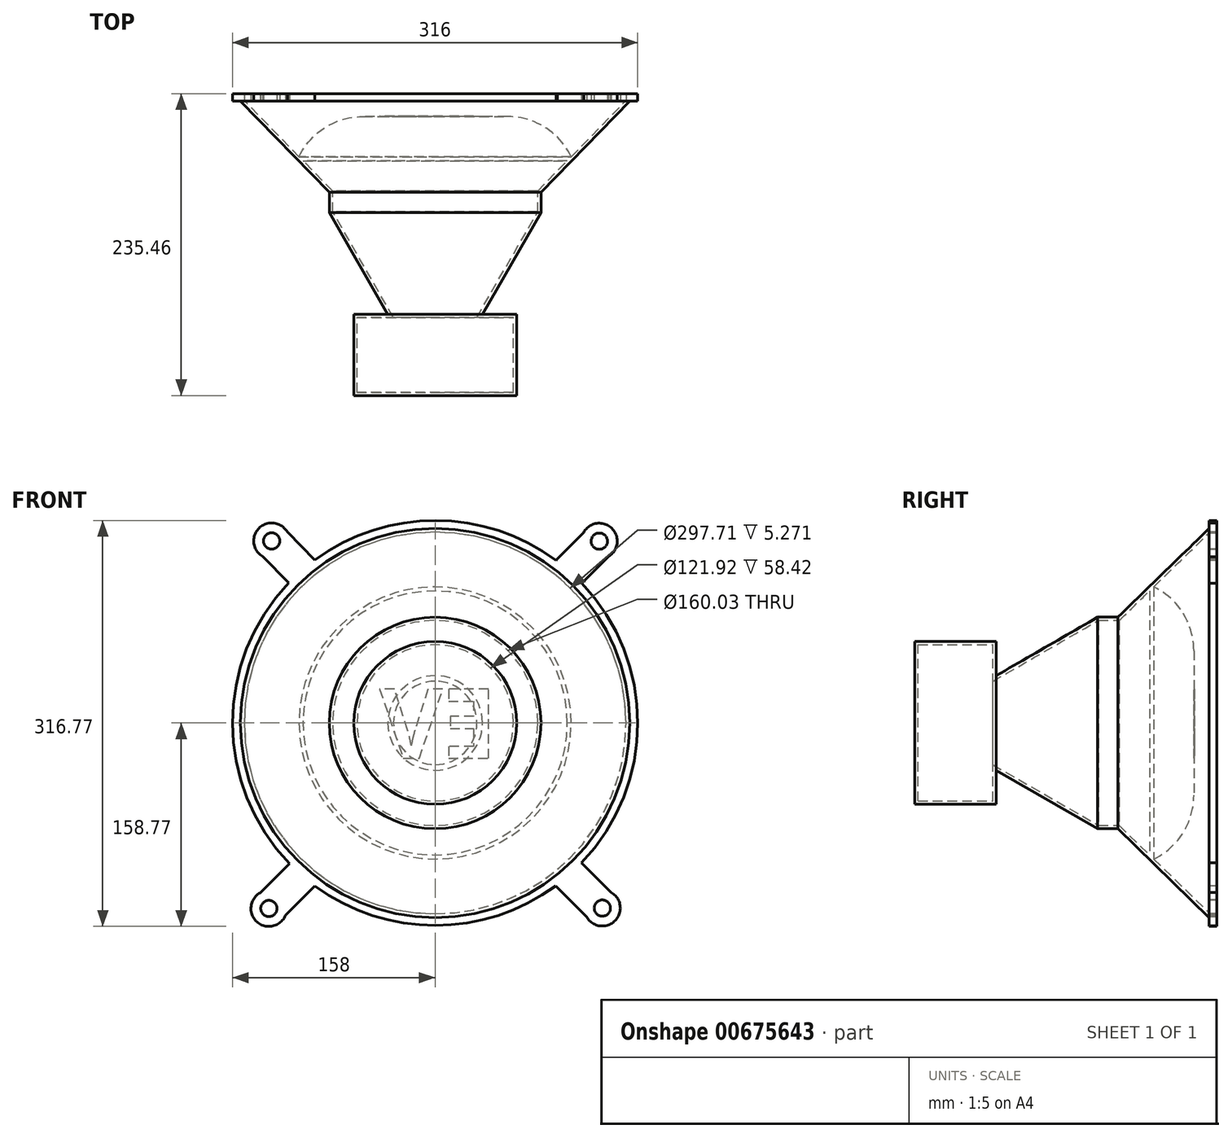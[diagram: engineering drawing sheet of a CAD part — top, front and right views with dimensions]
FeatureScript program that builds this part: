
annotation { "Feature Type Name" : "Feature", "Feature Type Description" : "" }
export const myFeature = defineFeature(function(context is Context, id is Id, definition is map)
    precondition{}
    {
        {
            var Q0;
            Q0=qCreatedBy(makeId("Front.planeOp"),FACE);
            var sketch = newSketch(context, id + "F0", { "sketchPlane" : qUnion([Q0])});
            skCircle(sketch, "E0", {"center": v(0, 0) * mm, "radius": 63.5 * mm});
            skSolve(sketch);
        }
        {
            var Q0;
            Q0 = qSketchRegion(id + "F0", true);
            extrude(context, id + "F1", {"entities" : qUnion([Q0]), "depth" : 63.5 * mm, "offsetDistance" : 25.4 * mm});
        }
        {
            var Q0;
            Q0=qCreatedBy(makeId("Right.planeOp"),FACE);
            var sketch = newSketch(context, id + "F2", { "sketchPlane" : qUnion([Q0])});
            skLineSegment(sketch, "E1", {"start": v(0, 36.92) * mm, "end": v(79.15, 82.55) * mm});
            skLineSegment(sketch, "E2", {"start": v(79.15, 82.55) * mm, "end": v(94.98, 82.55) * mm});
            skLineSegment(sketch, "E3", {"start": v(94.98, 82.55) * mm, "end": v(166.69, 152.4) * mm});
            skLineSegment(sketch, "E4", {"start": v(166.69, 152.4) * mm, "end": v(166.69, 0) * mm});
            skLineSegment(sketch, "E5", {"start": v(166.69, 0) * mm, "end": v(0, 0) * mm});
            skLineSegment(sketch, "E6", {"start": v(0, 0) * mm, "end": v(0, 36.92) * mm});
            skSolve(sketch);
        }
        {
            var Q0;
            Q0=makeQuery(id+"F2.imprint","IMPRINT",FACE,{"disambiguationData":[TD([[makeQuery(id+"F2.imprint","IMPRINT",EDGE,{"derivedFrom":sQuery(id+"F2.wireOp",EDGE,"E1")}),-1.0]])]});
            var Q1;
            Q1=sQuery(id+"F2.wireOp",EDGE,"E5");
            revolve(context, id + "F3", {"operationType" : NewBodyOperationType.ADD, "entities" : qUnion([Q0]), "axis" : qUnion([Q1]), "revolveType" : RevolveType.FULL});
        }
        {
            var Q0;
            Q0=makeQuery(id+"F3.opRevolve","SWEPT_FACE",FACE,{"disambiguationData":[OSD([sQuery(id+"F2.wireOp",EDGE,"E4")])]});
            shell(context, id + "F4", {"entities" : qUnion([Q0]), "thickness" : 2.54 * mm});
        }
        {
            var Q0;
            {var subQ0=sQuery(id+"F0.wireOp",EDGE,"E0");Q0=makeQuery(id+"F4.opShell","OFFSET_FACE",FACE,{"disambiguationData":[OSD([subQ0]),TDD([makeQuery(id+"F1.opExtrude","CAP_FACE",FACE,{"disambiguationData":[OSD([subQ0])],"isStart":false})])]});}
            var sketch = newSketch(context, id + "F5", { "sketchPlane" : qUnion([Q0])});
            skCircle(sketch, "E7", {"center": v(0, 0) * mm, "radius": 106.16 * mm});
            skSolve(sketch);
        }
        {
            var Q0;
            Q0 = qSketchRegion(id + "F5", true);
            extrude(context, id + "F6", {"entities" : qUnion([Q0]), "operationType" : NewBodyOperationType.ADD, "depth" : 215.14 * mm, "offsetDistance" : 25.4 * mm, "hasSecondDirection" : true, "secondDirectionOppositeDirection" : false, "secondDirectionDepth" : 180.6 * mm});
        }
        {
            var Q0;
            Q0=makeQuery(id+"F6.opExtrude","CAP_EDGE",EDGE,{"disambiguationData":[OSD([sQuery(id+"F5.wireOp",EDGE,"E7")])],"isStart":false});
            fillet(context, id + "F7", {"entities" : qUnion([Q0]), "radius" : 55.19 * mm, "tangentPropagation" : true, "allowEdgeOverflow" : false});
        }
        {
            var Q0;
            Q0=makeQuery(id+"F6.opExtrude","CAP_FACE",FACE,{"disambiguationData":[OSD([sQuery(id+"F5.wireOp",EDGE,"E7")])],"isStart":false});
            var sketch = newSketch(context, id + "F8", { "sketchPlane" : qUnion([Q0])});
            skText(sketch, "E8", { "text": "EV", "fontName": "OpenSans-Bold.ttf"});
            const initialGuessF8  = {"E8": [-0.04834, -0.02763, 1, 0, 0.05452]};
            skSetInitialGuess(sketch, initialGuessF8);
            skSolve(sketch);
        }
        {
            var Q0;
            Q0 = qSketchRegion(id + "F8", true);
            extrude(context, id + "F9", {"entities" : qUnion([Q0]), "operationType" : NewBodyOperationType.ADD, "depth" : 0.36 * mm, "offsetDistance" : 25.4 * mm});
        }
        {
            var Q0;
            Q0=qCreatedBy(makeId("Front.planeOp"),FACE);
            var sketch = newSketch(context, id + "F10", { "sketchPlane" : qUnion([Q0])});
            skCircle(sketch, "E9", {"center": v(0, 0) * mm, "radius": 148.85 * mm});
            skCircle(sketch, "E10", {"center": v(0, 0) * mm, "radius": 158 * mm});
            skLineSegment(sketch, "E11", {"start": v(137.91, 151.76) * mm, "end": v(104.63, 118.39) * mm});
            skLineSegment(sketch, "E12", {"start": v(-137.4, 151.97) * mm, "end": v(-104.32, 118.67) * mm});
            skLineSegment(sketch, "E13", {"start": v(140.22, 134.95) * mm, "end": v(114.36, 109.02) * mm});
            skLineSegment(sketch, "E14.MirrorCS", {"start": v(95.24, 128.09) * mm, "end": v(94.33, 126.75) * mm});
            skLineSegment(sketch, "E15.MirrorCS", {"start": v(121.1, 154.02) * mm, "end": v(95.24, 128.09) * mm});
            skLineSegment(sketch, "E16.MirrorCS", {"start": v(-139.73, 135.16) * mm, "end": v(-114.07, 109.32) * mm});
            skLineSegment(sketch, "E17.MirrorCS", {"start": v(-120.57, 154.19) * mm, "end": v(-93.75, 127.18) * mm});
            skCircle(sketch, "E18", {"center": v(128.02, 141.84) * mm, "radius": 14 * mm});
            skPoint(sketch, "E19.orphan", {"position": v(188.58, 183.45) * mm});
            skPoint(sketch, "E20.orphan", {"position": v(169.45, 202.51) * mm});
            skPoint(sketch, "E21.orphan", {"position": v(-187.56, 221.64) * mm});
            skPoint(sketch, "E22.orphan", {"position": v(-206.72, 202.61) * mm});
            skCircle(sketch, "E23", {"center": v(-127.52, 142.03) * mm, "radius": 14 * mm});
            skPoint(sketch, "E24.orphan", {"position": v(188.36, -159.6) * mm});
            skPoint(sketch, "E25.orphan", {"position": v(171.92, -175.92) * mm});
            skPoint(sketch, "E26.orphan", {"position": v(-170.14, -178.45) * mm});
            skPoint(sketch, "E27.orphan", {"position": v(-191.42, -157.24) * mm});
            skLineSegment(sketch, "E28.MirrorCS", {"start": v(-139.3, -135.4) * mm, "end": v(-113.66, -109.75) * mm});
            skLineSegment(sketch, "E29.MirrorCS", {"start": v(-137.24, -152) * mm, "end": v(-104.1, -118.86) * mm});
            skLineSegment(sketch, "E30.MirrorCS", {"start": v(-120.66, -154.1) * mm, "end": v(-93.75, -127.18) * mm});
            skCircle(sketch, "E31.MirrorC", {"center": v(-129.67, -144.77) * mm, "radius": 14 * mm});
            skLineSegment(sketch, "E32.MirrorCS", {"start": v(142.56, -137.58) * mm, "end": v(116.71, -111.69) * mm});
            skLineSegment(sketch, "E33.MirrorCS", {"start": v(123.46, -156.68) * mm, "end": v(97.62, -130.78) * mm});
            skLineSegment(sketch, "E34.MirrorCS", {"start": v(137.96, -151.71) * mm, "end": v(104.63, -118.39) * mm});
            skCircle(sketch, "E35.MirrorC", {"center": v(130.4, -144.47) * mm, "radius": 14 * mm});
            skPoint(sketch, "E36.orphan", {"position": v(98.16, 111.9) * mm});
            skPoint(sketch, "E37.orphan", {"position": v(98.15, -111.9) * mm});
            skPoint(sketch, "E38.orphan", {"position": v(-97.62, -112.38) * mm});
            skPoint(sketch, "E39.orphan", {"position": v(-97.86, 112.16) * mm});
            skPoint(sketch, "E40.orphan", {"position": v(-87.23, 120.62) * mm});
            skPoint(sketch, "E41.orphan", {"position": v(-107.62, 102.83) * mm});
            skPoint(sketch, "E42.orphan", {"position": v(188.82, 12.04) * mm});
            skPoint(sketch, "E43.orphan", {"position": v(-188.28, 12.05) * mm});
            skPoint(sketch, "E44.orphan", {"position": v(-8.82, 148.6) * mm});
            skPoint(sketch, "E45.start.orphan", {"position": v(-8.82, 0) * mm});
            skPoint(sketch, "E46.left.start.orphan", {"position": v(188.55, 202.54) * mm});
            skPoint(sketch, "E47.trimOffspring.end.orphan", {"position": v(189.1, -178.46) * mm});
            skPoint(sketch, "E46.right.start.orphan", {"position": v(-187.62, 202.55) * mm});
            skPoint(sketch, "E48.trimOffspring.end.orphan", {"position": v(-188.93, -178.45) * mm});
            skPoint(sketch, "E49.trimOffspring.start.orphan", {"position": v(-8.82, -148.6) * mm});
            skLineSegment(sketch, "E50", {"start": v(117.8, -112.77) * mm, "end": v(114.2, -109.18) * mm});
            skLineSegment(sketch, "E51", {"start": v(99.1, -132.26) * mm, "end": v(93.9, -127.06) * mm});
            skCircle(sketch, "E52", {"center": v(128.02, 141.84) * mm, "radius": 6.35 * mm});
            skCircle(sketch, "E53", {"center": v(-127.52, 142.03) * mm, "radius": 6.35 * mm});
            skCircle(sketch, "E54", {"center": v(-129.67, -144.77) * mm, "radius": 6.35 * mm});
            skCircle(sketch, "E55", {"center": v(130.4, -144.47) * mm, "radius": 6.35 * mm});
            skSolve(sketch);
        }
        {
            var Q0;
            Q0 = qSketchRegion(id + "F10", true);
            extrude(context, id + "F11", {"entities" : qUnion([Q0]), "operationType" : NewBodyOperationType.ADD, "oppositeDirection" : true, "depth" : 171.96 * mm, "offsetDistance" : 25.4 * mm, "hasSecondDirection" : true, "secondDirectionOppositeDirection" : true, "secondDirectionDepth" : 166.12 * mm});
        }
    });
